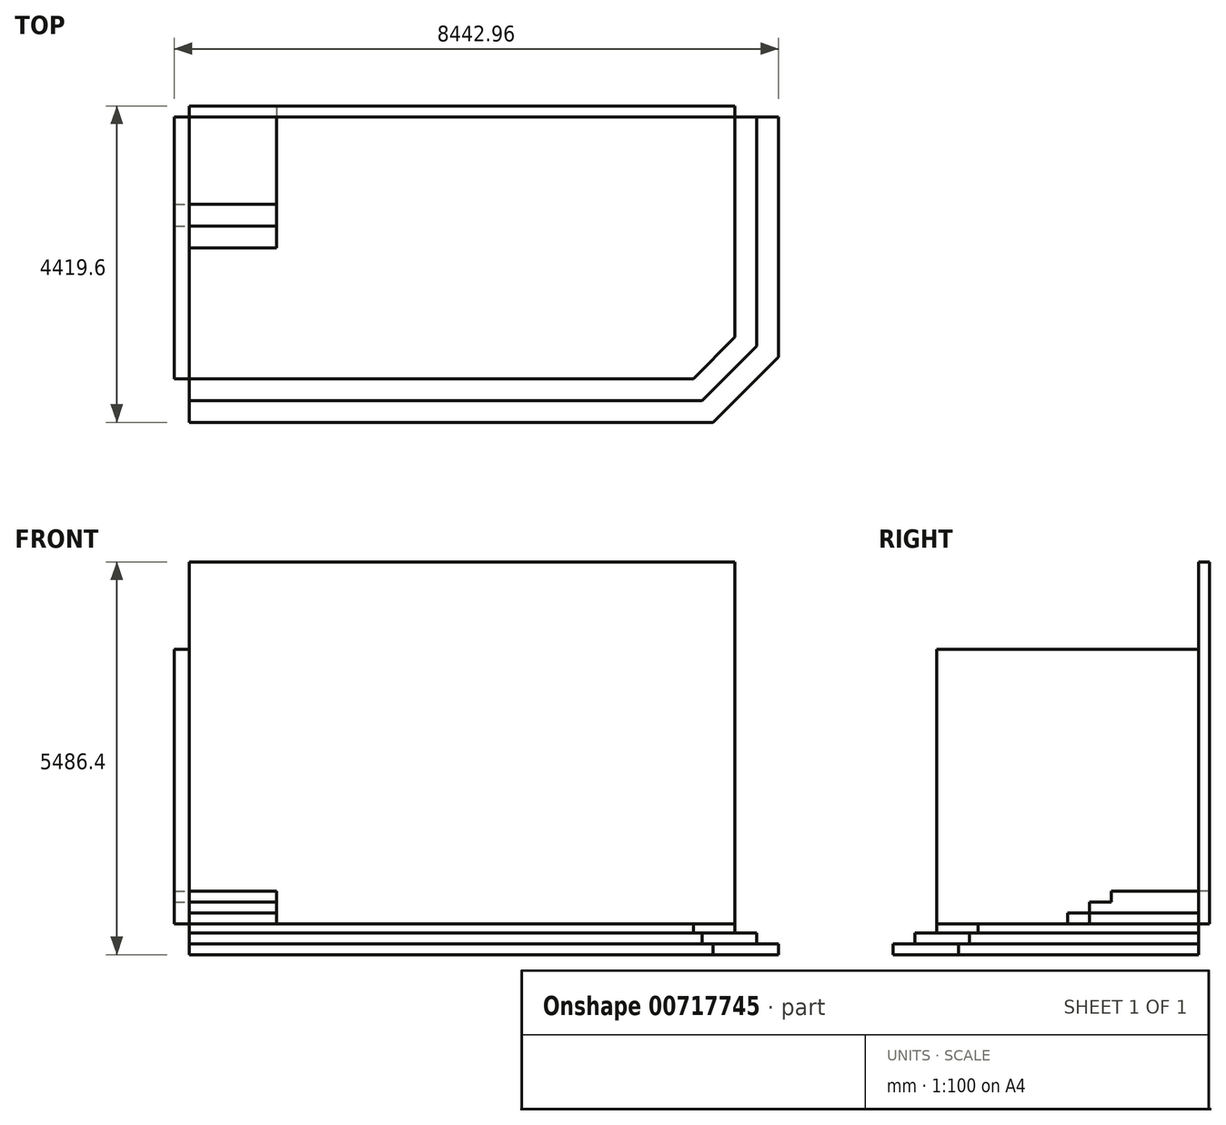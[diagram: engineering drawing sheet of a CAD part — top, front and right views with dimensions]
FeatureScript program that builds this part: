
annotation { "Feature Type Name" : "Feature", "Feature Type Description" : "" }
export const myFeature = defineFeature(function(context is Context, id is Id, definition is map)
    precondition{}
    {
        {
            var Q0;
            Q0=qCreatedBy(makeId("Top.planeOp"),FACE);
            var sketch = newSketch(context, id + "F0", { "sketchPlane" : qUnion([Q0])});
            skLineSegment(sketch, "E0.bottom", {"start": v(3810, -1828.8) * mm, "end": v(-3810, -1828.8) * mm});
            skLineSegment(sketch, "E0.top", {"start": v(3810, 1828.8) * mm, "end": v(-3810, 1828.8) * mm});
            skLineSegment(sketch, "E0.left", {"start": v(3810, -1828.8) * mm, "end": v(3810, 1828.8) * mm});
            skLineSegment(sketch, "E0.right", {"start": v(-3810, -1828.8) * mm, "end": v(-3810, 1828.8) * mm});
            skPoint(sketch, "E0.middle", {"position": v(0, 0) * mm});
            skSolve(sketch);
        }
        {
            var Q0;
            Q0=makeQuery(id+"F0.imprint","IMPRINT",FACE,{"disambiguationData":[TD([[makeQuery(id+"F0.imprint","IMPRINT",EDGE,{"derivedFrom":sQuery(id+"F0.wireOp",EDGE,"E0.bottom")}),-1.0]])]});
            extrude(context, id + "F1", {"entities" : qUnion([Q0]), "depth" : 426.72 * mm, "offsetDistance" : 30.48 * mm});
        }
        {
            var Q0;
            Q0=makeQuery(id+"F1.opExtrude","CAP_FACE",FACE,{"disambiguationData":[OSD([sQuery(id+"F0.wireOp",EDGE,"E0.bottom"),sQuery(id+"F0.wireOp",EDGE,"E0.top"),sQuery(id+"F0.wireOp",EDGE,"E0.left"),sQuery(id+"F0.wireOp",EDGE,"E0.right")])],"isStart":true});
            var sketch = newSketch(context, id + "F2", { "sketchPlane" : qUnion([Q0])});
            skLineSegment(sketch, "E1.bottom", {"start": v(-3810, -1828.8) * mm, "end": v(4419.6, -1828.8) * mm});
            skLineSegment(sketch, "E1.top", {"start": v(-3810, 2438.4) * mm, "end": v(4419.6, 2438.4) * mm});
            skLineSegment(sketch, "E1.left", {"start": v(-3810, -1828.8) * mm, "end": v(-3810, 2438.4) * mm});
            skLineSegment(sketch, "E1.right", {"start": v(4419.6, -1828.8) * mm, "end": v(4419.6, 2438.4) * mm});
            skSolve(sketch);
        }
        {
            var Q0;
            Q0 = qSketchRegion(id + "F2", true);
            extrude(context, id + "F3", {"entities" : qUnion([Q0]), "operationType" : NewBodyOperationType.ADD, "oppositeDirection" : true, "depth" : 152.4 * mm, "offsetDistance" : 30.48 * mm});
        }
        {
            var Q0;
            {var subQ4=sQuery(id+"F2.wireOp",EDGE,"E1.top");Q0=makeQuery(id+"F2.imprint","IMPRINT",FACE,{"disambiguationData":[TD([[makeQuery(id+"F2.imprint","IMPRINT",EDGE,{"derivedFrom":subQ4}),-1.0]])]});}
            extrude(context, id + "F4", {"entities" : qUnion([Q0]), "operationType" : NewBodyOperationType.ADD, "oppositeDirection" : true, "depth" : 152.4 * mm, "offsetDistance" : 30.48 * mm});
        }
        {
            var Q0;
            Q0=makeQuery(id+"F1.opExtrude","CAP_FACE",FACE,{"disambiguationData":[OSD([sQuery(id+"F0.wireOp",EDGE,"E0.bottom"),sQuery(id+"F0.wireOp",EDGE,"E0.top"),sQuery(id+"F0.wireOp",EDGE,"E0.left"),sQuery(id+"F0.wireOp",EDGE,"E0.right")])],"isStart":false});
            var sketch = newSketch(context, id + "F5", { "sketchPlane" : qUnion([Q0])});
            skLineSegment(sketch, "E2.bottom", {"start": v(-3810, 1828.8) * mm, "end": v(-2590.8, 1828.8) * mm});
            skLineSegment(sketch, "E2.top", {"start": v(-3810, 609.6) * mm, "end": v(-2590.8, 609.6) * mm});
            skLineSegment(sketch, "E2.left", {"start": v(-3810, 1828.8) * mm, "end": v(-3810, 609.6) * mm});
            skLineSegment(sketch, "E2.right", {"start": v(-2590.8, 1828.8) * mm, "end": v(-2590.8, 609.6) * mm});
            skSolve(sketch);
        }
        {
            var Q0;
            Q0=makeQuery(id+"F5.imprint","IMPRINT",FACE,{"disambiguationData":[TD([[makeQuery(id+"F5.imprint","IMPRINT",EDGE,{"derivedFrom":sQuery(id+"F5.wireOp",EDGE,"E2.bottom")}),1.0]])]});
            extrude(context, id + "F6", {"entities" : qUnion([Q0]), "operationType" : NewBodyOperationType.ADD, "depth" : 457.2 * mm, "offsetDistance" : 30.48 * mm});
        }
        {
            var Q0;
            {var subQ0=sQuery(id+"F0.wireOp",EDGE,"E0.right");var subQ1=sQuery(id+"F0.wireOp",EDGE,"E0.left");var subQ2=sQuery(id+"F0.wireOp",EDGE,"E0.top");var subQ3=sQuery(id+"F0.wireOp",EDGE,"E0.bottom");Q0=makeQuery(id+"F4.boolean.opBoolean","MERGE",FACE,{"derivedFrom":[makeQuery(id+"F1.opExtrude","CAP_FACE",FACE,{"disambiguationData":[OSD([subQ3,subQ2,subQ1,subQ0])],"isStart":true}),makeQuery(id+"F4.opExtrude","CAP_FACE",FACE,{"disambiguationData":[OSD([subQ3,subQ2,subQ1,subQ0,sQuery(id+"F2.wireOp",EDGE,"E1.bottom"),sQuery(id+"F2.wireOp",EDGE,"E1.top"),sQuery(id+"F2.wireOp",EDGE,"E1.left"),sQuery(id+"F2.wireOp",EDGE,"E1.right")])],"isStart":true})]});}
            var sketch = newSketch(context, id + "F7", { "sketchPlane" : qUnion([Q0])});
            skLineSegment(sketch, "E3.bottom", {"start": v(-3810, -1828.8) * mm, "end": v(-2590.8, -1828.8) * mm});
            skLineSegment(sketch, "E3.top", {"start": v(-3810, -304.8) * mm, "end": v(-2590.8, -304.8) * mm});
            skLineSegment(sketch, "E3.left", {"start": v(-3810, -1828.8) * mm, "end": v(-3810, -304.8) * mm});
            skLineSegment(sketch, "E3.right", {"start": v(-2590.8, -1828.8) * mm, "end": v(-2590.8, -304.8) * mm});
            skSolve(sketch);
        }
        {
            var Q0;
            Q0=makeQuery(id+"F7.imprint","IMPRINT",FACE,{"disambiguationData":[TD([[makeQuery(id+"F7.imprint","IMPRINT",EDGE,{"derivedFrom":sQuery(id+"F7.wireOp",EDGE,"E3.bottom")}),-1.0]])]});
            extrude(context, id + "F8", {"entities" : qUnion([Q0]), "operationType" : NewBodyOperationType.ADD, "oppositeDirection" : true, "depth" : 731.52 * mm, "offsetDistance" : 30.48 * mm});
        }
        {
            var Q0;
            Q0=makeQuery(id+"F6.boolean.opBoolean","MERGE",FACE,{"derivedFrom":[makeQuery(id+"F3.boolean.opBoolean","MERGE",FACE,{"derivedFrom":[makeQuery(id+"F1.opExtrude","SWEPT_FACE",FACE,{"disambiguationData":[OSD([sQuery(id+"F0.wireOp",EDGE,"E0.top")])]}),makeQuery(id+"F3.opExtrude","SWEPT_FACE",FACE,{"disambiguationData":[OSD([sQuery(id+"F2.wireOp",EDGE,"E1.bottom")])]})]}),makeQuery(id+"F6.opExtrude","SWEPT_FACE",FACE,{"disambiguationData":[OSD([sQuery(id+"F5.wireOp",EDGE,"E2.bottom")])]})]});
            var sketch = newSketch(context, id + "F9", { "sketchPlane" : qUnion([Q0])});
            skLineSegment(sketch, "E4.bottom", {"start": v(3810, 0) * mm, "end": v(-3810, 0) * mm});
            skLineSegment(sketch, "E4.top", {"start": v(3810, 5486.4) * mm, "end": v(-3810, 5486.4) * mm});
            skLineSegment(sketch, "E4.left", {"start": v(3810, 0) * mm, "end": v(3810, 5486.4) * mm});
            skLineSegment(sketch, "E4.right", {"start": v(-3810, 0) * mm, "end": v(-3810, 5486.4) * mm});
            skSolve(sketch);
        }
        {
            var Q0;
            {var subQ5=sQuery(id+"F9.wireOp",EDGE,"E4.top");Q0=makeQuery(id+"F9.imprint","IMPRINT",FACE,{"disambiguationData":[TD([[makeQuery(id+"F9.imprint","IMPRINT",EDGE,{"derivedFrom":subQ5}),1.0]])]});}
            extrude(context, id + "F10", {"entities" : qUnion([Q0]), "depth" : 152.4 * mm, "offsetDistance" : 30.48 * mm});
        }
        {
            var Q0;
            Q0=makeQuery(id+"F8.boolean.opBoolean","MERGE",FACE,{"derivedFrom":[makeQuery(id+"F6.boolean.opBoolean","MERGE",FACE,{"derivedFrom":[makeQuery(id+"F4.boolean.opBoolean","MERGE",FACE,{"derivedFrom":[makeQuery(id+"F1.opExtrude","SWEPT_FACE",FACE,{"disambiguationData":[OSD([sQuery(id+"F0.wireOp",EDGE,"E0.right")])]}),makeQuery(id+"F4.opExtrude","SWEPT_FACE",FACE,{"disambiguationData":[OSD([sQuery(id+"F2.wireOp",EDGE,"E1.left")])]})]}),makeQuery(id+"F6.opExtrude","SWEPT_FACE",FACE,{"disambiguationData":[OSD([sQuery(id+"F5.wireOp",EDGE,"E2.left")])]})]}),makeQuery(id+"F8.opExtrude","SWEPT_FACE",FACE,{"disambiguationData":[OSD([sQuery(id+"F7.wireOp",EDGE,"E3.left")])]})]});
            var sketch = newSketch(context, id + "F11", { "sketchPlane" : qUnion([Q0])});
            skLineSegment(sketch, "E5.bottom", {"start": v(-1828.8, 0) * mm, "end": v(1828.8, 0) * mm});
            skLineSegment(sketch, "E5.top", {"start": v(-1828.8, 4267.2) * mm, "end": v(1828.8, 4267.2) * mm});
            skLineSegment(sketch, "E5.left", {"start": v(-1828.8, 0) * mm, "end": v(-1828.8, 4267.2) * mm});
            skLineSegment(sketch, "E5.right", {"start": v(1828.8, 0) * mm, "end": v(1828.8, 4267.2) * mm});
            skSolve(sketch);
        }
        {
            var Q0;
            {var subQ5=sQuery(id+"F11.wireOp",EDGE,"E5.top");Q0=makeQuery(id+"F11.imprint","IMPRINT",FACE,{"disambiguationData":[TD([[makeQuery(id+"F11.imprint","IMPRINT",EDGE,{"derivedFrom":subQ5}),-1.0]])]});}
            extrude(context, id + "F12", {"entities" : qUnion([Q0]), "depth" : 213.36 * mm, "offsetDistance" : 30.48 * mm});
        }
        {
            var Q0;
            Q0=makeQuery(id+"F3.opExtrude","CAP_FACE",FACE,{"disambiguationData":[OSD([sQuery(id+"F2.wireOp",EDGE,"E1.bottom"),sQuery(id+"F2.wireOp",EDGE,"E1.top"),sQuery(id+"F2.wireOp",EDGE,"E1.left"),sQuery(id+"F2.wireOp",EDGE,"E1.right")])],"isStart":false});
            var sketch = newSketch(context, id + "F13", { "sketchPlane" : qUnion([Q0])});
            skLineSegment(sketch, "E6.bottom", {"start": v(-3810, 1828.8) * mm, "end": v(4114.8, 1828.8) * mm});
            skLineSegment(sketch, "E6.top", {"start": v(-3810, -2133.6) * mm, "end": v(4114.8, -2133.6) * mm});
            skLineSegment(sketch, "E6.left", {"start": v(-3810, 1828.8) * mm, "end": v(-3810, -2133.6) * mm});
            skLineSegment(sketch, "E6.right", {"start": v(4114.8, 1828.8) * mm, "end": v(4114.8, -2133.6) * mm});
            skSolve(sketch);
        }
        {
            var Q0;
            {var subQ2=sQuery(id+"F2.wireOp",EDGE,"E1.bottom");var subQ4=sQuery(id+"F2.wireOp",EDGE,"E1.right");var subQ5=sQuery(id+"F2.wireOp",EDGE,"E1.left");var subQ6=sQuery(id+"F2.wireOp",EDGE,"E1.top");var subQ7=makeQuery(id+"F3.opExtrude","CAP_FACE",FACE,{"disambiguationData":[OSD([subQ2,subQ6,subQ5,subQ4])],"isStart":false});var subQ13=sQuery(id+"F0.wireOp",EDGE,"E0.bottom");var subQ14=makeQuery(id+"F3.boolean.opBoolean","INTERSECT",EDGE,{"derivedFrom":[makeQuery(id+"F1.opExtrude","SWEPT_FACE",FACE,{"disambiguationData":[OSD([subQ13])]}),subQ7]});Q0=makeQuery(id+"F13.imprint","IMPRINT",FACE,{"disambiguationData":[TD([[makeQuery(id+"F13.imprint","IMPRINT",EDGE,{"derivedFrom":subQ14}),-1.0]])]});}
            extrude(context, id + "F14", {"entities" : qUnion([Q0]), "operationType" : NewBodyOperationType.ADD, "depth" : 152.4 * mm, "offsetDistance" : 30.48 * mm});
        }
        {
            var Q0;
            Q0=makeQuery(id+"F1.opExtrude","SWEPT_EDGE",EDGE,{"disambiguationData":[OSD([sQuery(id+"F0.wireOp",EDGE,"E0.bottom"),sQuery(id+"F0.wireOp",EDGE,"E0.left")])]});
            chamfer(context, id + "F15", {"entities" : qUnion([Q0]), "width" : 579.12 * mm, "tangentPropagation" : true});
        }
        {
            var Q0;
            Q0=makeQuery(id+"F14.opExtrude","SWEPT_EDGE",EDGE,{"disambiguationData":[OSD([sQuery(id+"F13.wireOp",EDGE,"E6.top"),sQuery(id+"F13.wireOp",EDGE,"E6.right")])]});
            chamfer(context, id + "F16", {"entities" : qUnion([Q0]), "width" : 762 * mm, "tangentPropagation" : true});
        }
        {
            var Q0;
            Q0=makeQuery(id+"F1.opExtrude","CAP_FACE",FACE,{"disambiguationData":[OSD([sQuery(id+"F0.wireOp",EDGE,"E0.bottom"),sQuery(id+"F0.wireOp",EDGE,"E0.top"),sQuery(id+"F0.wireOp",EDGE,"E0.left"),sQuery(id+"F0.wireOp",EDGE,"E0.right")])],"isStart":false});
            var sketch = newSketch(context, id + "F17", { "sketchPlane" : qUnion([Q0])});
            skLineSegment(sketch, "E7.bottom", {"start": v(-3810, 1828.8) * mm, "end": v(-2590.8, 1828.8) * mm});
            skLineSegment(sketch, "E7.top", {"start": v(-3810, 0) * mm, "end": v(-2590.8, 0) * mm});
            skLineSegment(sketch, "E7.left", {"start": v(-3810, 1828.8) * mm, "end": v(-3810, 0) * mm});
            skLineSegment(sketch, "E7.right", {"start": v(-2590.8, 1828.8) * mm, "end": v(-2590.8, 0) * mm});
            skSolve(sketch);
        }
        {
            var Q0;
            Q0 = qSketchRegion(id + "F17", true);
            extrude(context, id + "F18", {"entities" : qUnion([Q0]), "depth" : 152.4 * mm, "offsetDistance" : 30.48 * mm});
        }
        {
            var Q0;
            Q0=makeQuery(id+"F3.opExtrude","SWEPT_EDGE",EDGE,{"disambiguationData":[OSD([sQuery(id+"F2.wireOp",EDGE,"E1.top"),sQuery(id+"F2.wireOp",EDGE,"E1.right")])]});
            chamfer(context, id + "F19", {"entities" : qUnion([Q0]), "width" : 914.4 * mm, "tangentPropagation" : true});
        }
    });
